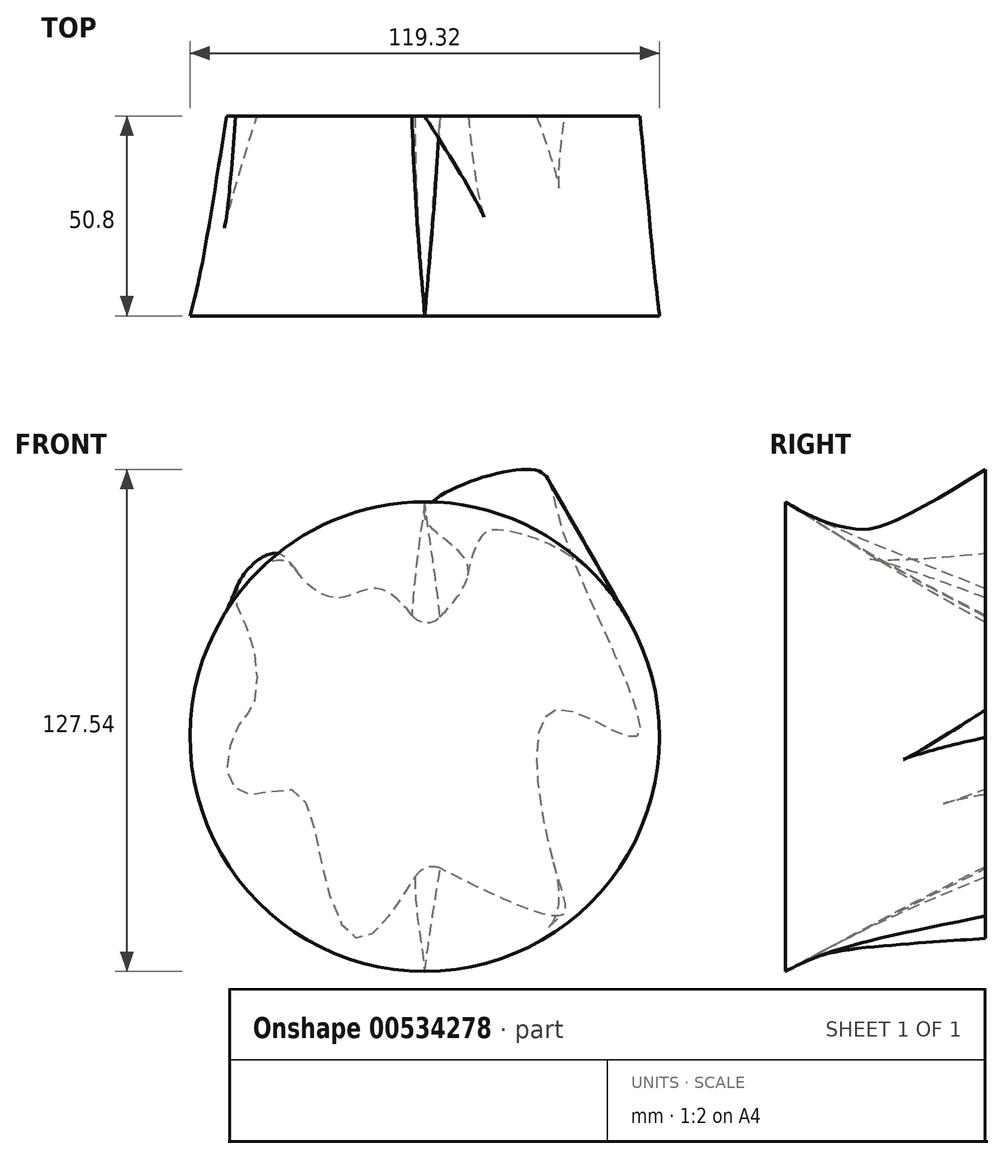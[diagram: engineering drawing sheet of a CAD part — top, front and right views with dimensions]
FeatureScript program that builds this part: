
annotation { "Feature Type Name" : "Feature", "Feature Type Description" : "" }
export const myFeature = defineFeature(function(context is Context, id is Id, definition is map)
    precondition{}
    {
        {
            var Q0;
            Q0=qCreatedBy(makeId("Front.planeOp"),FACE);
            var sketch = newSketch(context, id + "F0", { "sketchPlane" : qUnion([Q0])});
            skFitSpline(sketch, "E0", {"points": [v(0, 26.57) * mm, v(-11.9, 37.6) * mm, v(-21.78, 35.29) * mm, v(-31.07, 40.22) * mm, v(-38.04, 46.61) * mm, v(-47.92, 37.32) * mm, v(-44.14, 24.83) * mm, v(-43.56, 7.99) * mm, v(-46.47, 4.21) * mm, v(-50.24, -9.15) * mm, v(-44.14, -14.67) * mm, v(-32.82, -13.8) * mm, v(-25.56, -35.29) * mm, v(-16.84, -51.26) * mm, v(-7.26, -43.13) * mm, v(0, -31.51) * mm], "startDerivative": vector(-155.48, 208.62) * mm, "endDerivative": vector(92.61, 160.52) * mm});
            skFitSpline(sketch, "E1", {"points": [v(0, 26.57) * mm, v(10.53, 44.53) * mm, v(0, 56.84) * mm, v(27.4, 67.8) * mm, v(34.7, 53.2) * mm, v(53.87, 0) * mm, v(32.88, 6.67) * mm, v(32.43, -31.2) * mm, v(34.7, -45.33) * mm, v(0, -31.51) * mm], "startDerivative": vector(197.75, 194.43) * mm, "endDerivative": vector(-353.12, 177.7) * mm});
            skSolve(sketch);
        }
        {
            var Q0;
            Q0=qCreatedBy(makeId("Front.planeOp"),FACE);
            cPlane(context, id + "F1", {"entities" : qUnion([Q0]), "cplaneType" : CPlaneType.OFFSET, "offset" : 50.8 * mm, "width" : 152.4 * mm, "height" : 152.4 * mm});
        }
        {
            var Q0;
            Q0=qCreatedBy(id+"F1.planeOp",FACE);
            var sketch = newSketch(context, id + "F2", { "sketchPlane" : qUnion([Q0])});
            skCircle(sketch, "E2", {"center": v(0, 0) * mm, "radius": 59.66 * mm});
            skSolve(sketch);
        }
        {
            var Q0;
            Q0=makeQuery(id+"F0.imprint","IMPRINT",FACE,{"disambiguationData":[TD([[makeQuery(id+"F0.imprint","IMPRINT",EDGE,{"derivedFrom":sQuery(id+"F0.wireOp",EDGE,"E0")}),1.0]])]});
            var Q1;
            Q1=makeQuery(id+"F2.imprint","IMPRINT",FACE,{"disambiguationData":[TD([[makeQuery(id+"F2.imprint","IMPRINT",EDGE,{"derivedFrom":sQuery(id+"F2.wireOp",EDGE,"E2")}),1.0]])]});
            loft(context, id + "F3", {"sheetProfilesArray" : [{ "sheetProfileEntities" : qUnion([Q0]) }, { "sheetProfileEntities" : qUnion([Q1]) }]});
        }
        {
            var Q0;
            Q0=makeQuery(id+"F3.opLoft","SWEPT_EDGE",EDGE,{"disambiguationData":[OSD([sQuery(id+"F0.wireOp",EDGE,"E0"),sQuery(id+"F0.wireOp",EDGE,"E1"),sQuery(id+"F2.wireOp",EDGE,"E2")])]});
            var Q1;
            Q1=makeQuery(id+"F3.opLoft","SWEPT_EDGE",EDGE,{"disambiguationData":[OSD([sQuery(id+"F0.wireOp",EDGE,"E0"),sQuery(id+"F0.wireOp",EDGE,"E1")])]});
            fillet(context, id + "F4", {"entities" : qUnion([Q0, Q1]), "radius" : 5.08 * mm, "tangentPropagation" : true, "allowEdgeOverflow" : false});
        }
    });
